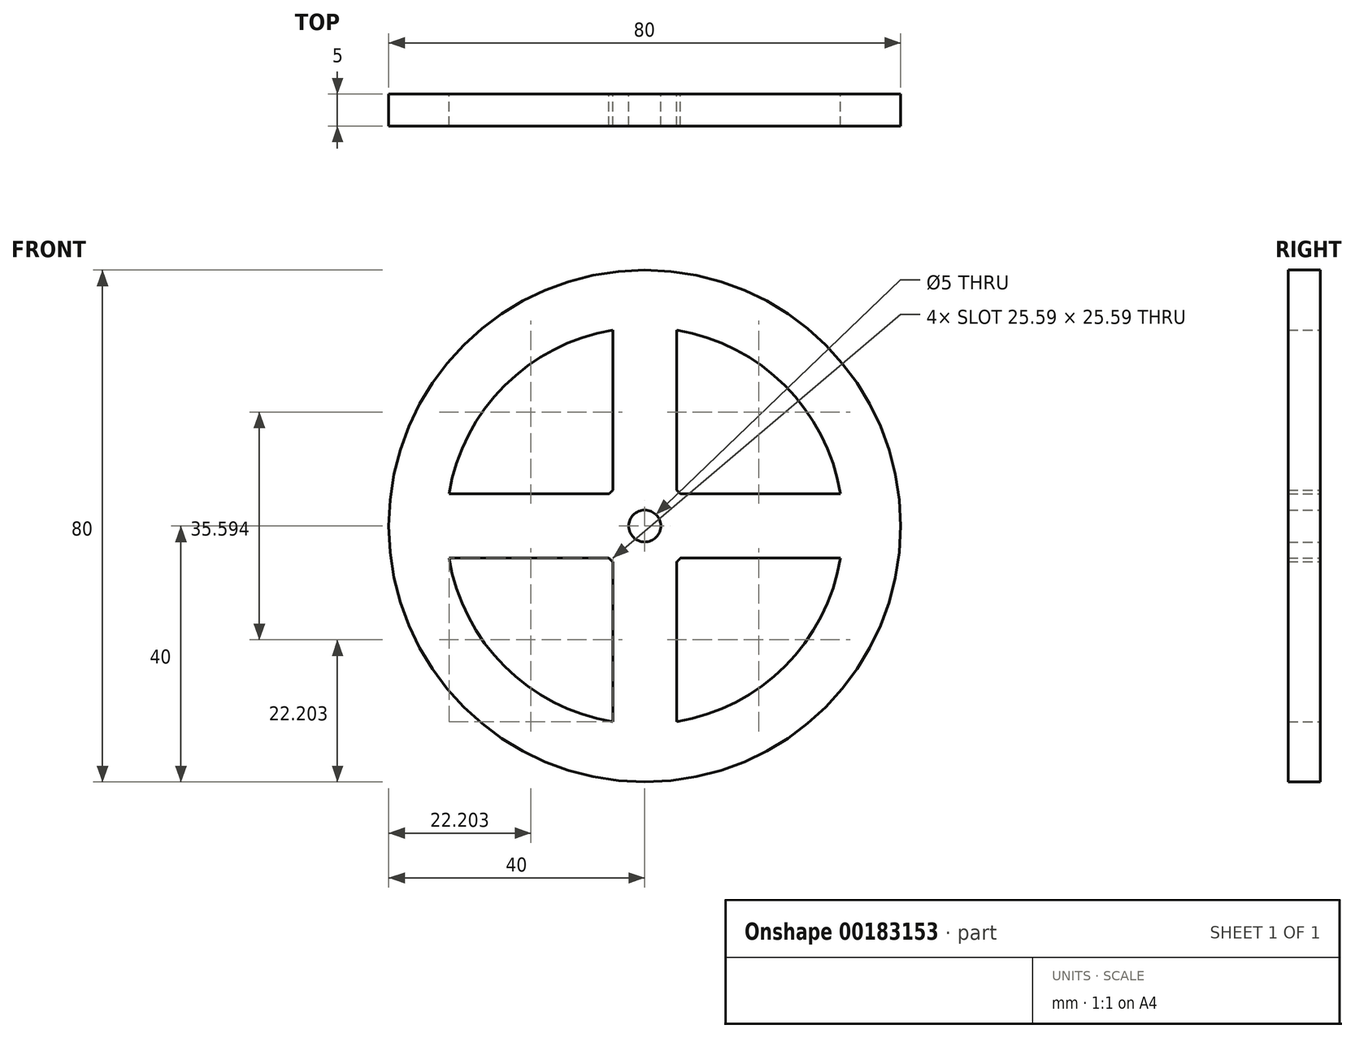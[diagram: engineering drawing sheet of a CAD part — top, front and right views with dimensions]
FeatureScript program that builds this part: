
annotation { "Feature Type Name" : "Feature", "Feature Type Description" : "" }
export const myFeature = defineFeature(function(context is Context, id is Id, definition is map)
    precondition{}
    {
        {
            var Q0;
            Q0=qCreatedBy(makeId("Front.planeOp"),FACE);
            var sketch = newSketch(context, id + "F0", { "sketchPlane" : qUnion([Q0])});
            skCircle(sketch, "E0", {"center": v(0, 0) * mm, "radius": 40 * mm});
            skCircle(sketch, "E1", {"center": v(0, 0) * mm, "radius": 2.5 * mm});
            skLineSegment(sketch, "E2", {"start": v(0, 0) * mm, "end": v(0, 31) * mm, "construction": true});
            skLineSegment(sketch, "E3", {"start": v(0, 0) * mm, "end": v(31, 0) * mm, "construction": true});
            skLineSegment(sketch, "E4", {"start": v(0, 0) * mm, "end": v(0, -31) * mm, "construction": true});
            skLineSegment(sketch, "E5", {"start": v(0, 0) * mm, "end": v(-31, 0) * mm, "construction": true});
            skArc(sketch, "E6", {"start": v(-5, 30.6) * mm, "mid": v(-21.92, 21.92) * mm, "end": v(-30.6, 5) * mm});
            skArc(sketch, "E7", {"start": v(5, -30.6) * mm, "mid": v(21.92, -21.92) * mm, "end": v(30.6, -5) * mm});
            skArc(sketch, "E8.trimOffspring", {"start": v(-30.6, -5) * mm, "mid": v(-21.92, -21.92) * mm, "end": v(-5, -30.6) * mm});
            skArc(sketch, "E9.trimOffspring", {"start": v(30.6, 5) * mm, "mid": v(21.92, 21.92) * mm, "end": v(5, 30.6) * mm});
            skLineSegment(sketch, "E10.trimOffspring", {"start": v(-5.6, 5) * mm, "end": v(-30.6, 5) * mm});
            skLineSegment(sketch, "E11.trimOffspring", {"start": v(-5, 5.6) * mm, "end": v(-5, 5.6) * mm});
            skLineSegment(sketch, "E12.trimOffspring", {"start": v(5.6, 5) * mm, "end": v(5.6, 5) * mm});
            skLineSegment(sketch, "E13.trimOffspring", {"start": v(5, 5.6) * mm, "end": v(5, 30.6) * mm});
            skLineSegment(sketch, "E14.trimOffspring", {"start": v(5.6, -5) * mm, "end": v(30.6, -5) * mm});
            skLineSegment(sketch, "E15.trimOffspring", {"start": v(5, -5.6) * mm, "end": v(5, -30.6) * mm});
            skLineSegment(sketch, "E16.trimOffspring", {"start": v(-5, -5.6) * mm, "end": v(-5, -30.6) * mm});
            skLineSegment(sketch, "E17.trimOffspring", {"start": v(-5.6, -5) * mm, "end": v(-30.6, -5) * mm});
            skArc(sketch, "E18", {"start": v(-5.6, -5) * mm, "mid": v(-5.3, -5.3) * mm, "end": v(-5, -5.6) * mm});
            skArc(sketch, "E19", {"start": v(-5, 5.6) * mm, "mid": v(-5.3, 5.3) * mm, "end": v(-5.6, 5) * mm});
            skArc(sketch, "E20", {"start": v(5.62, 4.97) * mm, "mid": v(5.32, 5.29) * mm, "end": v(5, 5.6) * mm});
            skLineSegment(sketch, "E21", {"start": v(5, -5.6) * mm, "end": v(5, -5.6) * mm});
            skArc(sketch, "E22", {"start": v(5, -5.6) * mm, "mid": v(5.3, -5.3) * mm, "end": v(5.6, -5) * mm});
            skLineSegment(sketch, "E23", {"start": v(5, 5.6) * mm, "end": v(5, 5.6) * mm});
            skLineSegment(sketch, "E24", {"start": v(5.6, 5) * mm, "end": v(30.6, 5) * mm});
            skLineSegment(sketch, "E25", {"start": v(-5, 5.6) * mm, "end": v(-5, 30.6) * mm});
            skLineSegment(sketch, "E26", {"start": v(-5.6, 5) * mm, "end": v(-5.6, 5) * mm});
            skSolve(sketch);
        }
        {
            var Q0;
            Q0=makeQuery(id+"F0.imprint","IMPRINT",FACE,{"disambiguationData":[TD([[makeQuery(id+"F0.imprint","IMPRINT",EDGE,{"derivedFrom":sQuery(id+"F0.wireOp",EDGE,"E0")}),1.0]])]});
            extrude(context, id + "F1", {"entities" : qUnion([Q0]), "endBound" : BoundingType.SYMMETRIC, "depth" : 5 * mm});
        }
    });
